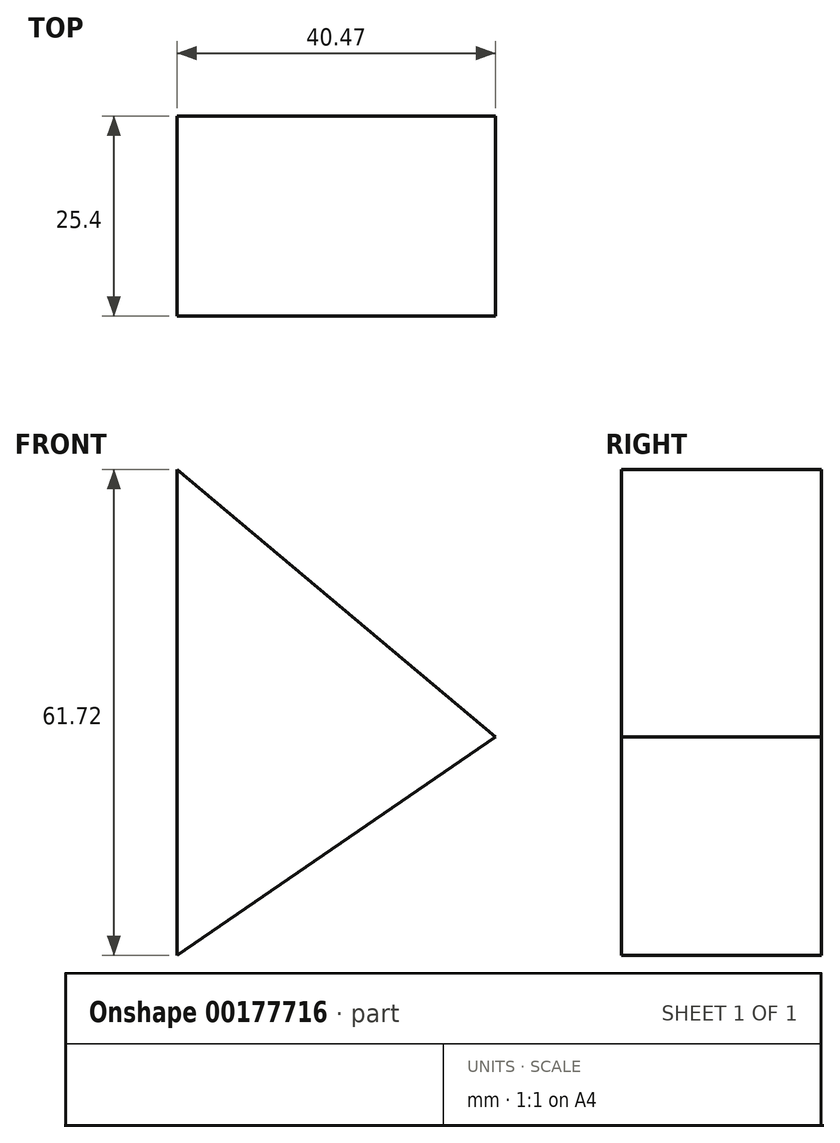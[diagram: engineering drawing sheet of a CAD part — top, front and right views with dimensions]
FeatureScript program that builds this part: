
annotation { "Feature Type Name" : "Feature", "Feature Type Description" : "" }
export const myFeature = defineFeature(function(context is Context, id is Id, definition is map)
    precondition{}
    {
        {
            var Q0;
            Q0=qCreatedBy(makeId("Front.planeOp"),FACE);
            var sketch = newSketch(context, id + "F0", { "sketchPlane" : qUnion([Q0])});
            skLineSegment(sketch, "E0", {"start": v(-35.7, 33.96) * mm, "end": v(-35.7, -27.76) * mm});
            skLineSegment(sketch, "E1", {"start": v(-35.7, 33.96) * mm, "end": v(4.77, 0) * mm});
            skLineSegment(sketch, "E2", {"start": v(4.77, 0) * mm, "end": v(-35.7, -27.76) * mm});
            skSolve(sketch);
        }
        {
            var Q0;
            Q0=makeQuery(id+"F0.imprint","IMPRINT",FACE,{"disambiguationData":[TD([[makeQuery(id+"F0.imprint","IMPRINT",EDGE,{"derivedFrom":sQuery(id+"F0.wireOp",EDGE,"E0")}),1.0]])]});
            extrude(context, id + "F1", {"entities" : qUnion([Q0]), "depth" : 25.4 * mm});
        }
    });
